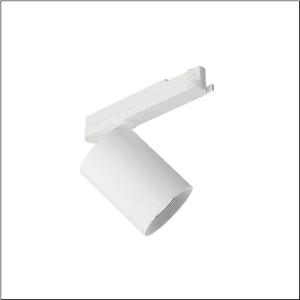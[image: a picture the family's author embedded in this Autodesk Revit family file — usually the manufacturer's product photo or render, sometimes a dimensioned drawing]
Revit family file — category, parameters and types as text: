
# Revit family: spot_21_51se13mbd5b
name_source: partatom
category: Lighting Fixtures
units: mm (PartAtom-declared; Revit-internal decimal feet)

## family parameters
Cut with Voids When Loaded = No
Host = Face
Light Source = No
Part Type = Normal
Room Calculation Point = No
Round Connector Dimension = Use Diameter
Shared = No

## types (1)
- --- (1 x LED, 5520 lm, 41.5 W, 4000K)
    Apparent Load = 42 VA
    CIE Flux Codes = 95 98 99 100 100
    Color Rendering = 90
    Color Temperature = 4000K
    Default Elevation = 1800 mm
    Description = Spot 21, directional spotlight, light control with lens, of PMMA, LED rated luminous flux: 5.300lm, light colour: 940, control gear: ECG Multilumen, with 3-phase adapter, mains connection: 220..240V, AC, 50/60Hz, of aluminium, traffic white (RAL 9016), length: 213mm, diameter: 105mm, protection rating (complete): IP20, insulation class (complete): insulation class I (protective earthing), certification: CE, impact resistance: IK02, permissible ambient temperature for indoor applications: -20..+40°C, packaging unit: 1 piece
    Height = 175 mm
    Lamp = 1 x LED
    Lamp Light Flux = 5520 lm
    Lamp Power = 41.5 W
    Lamp count = 1
    Length = 105 mm
    Luminous efficacy = 133 lm/W
    Manufacturer = Siteco
    ModVariant = No
    Model = 51SE13MBD5B
    Mounting Place = Ceiling
    Mounting Type = Pendant
    Number of Poles = 1
    OnlyDefault = Yes
    Power Factor = 1
    Product Name = Spot 21
    Product group = directional spotlight
    ProductGroupID = 905
    Protection Class = Protection class I
    Protection Degree = IP 20
    RLX_Detail_Level = 1
    RLX_Emergency_Light_Flux = 0 lm
    RLX_Emergency_Type = 0
    RLX_Emergency_Type_DB = No
    RlxData = <blob elided: 17605 chars, md5=96a970d0>
    Socket = socket
    Standby Power = 0 W
    System Light Flux = 5520 lm
    System Power = 42 W
    Type Comments = factory setting: luminous flux: 100 % | (ON | ON | ON | ON) | 1050 mA
    Type Image = l_1003976.jpg
    URL = http://relux.com
    VarID = @adj_075701
    Voltage = 0 V
    Weight = 0.00 kg
    Width = 0 mm  [stored 0 ft]

note: [stored X ft] marks values corroborated as IEEE doubles in the binary element streams (Revit-internal decimal feet)

## geometry (parser evidence)
native form markers: Blend x4, Sweep x11
no freeform markers — native parametric forms only
